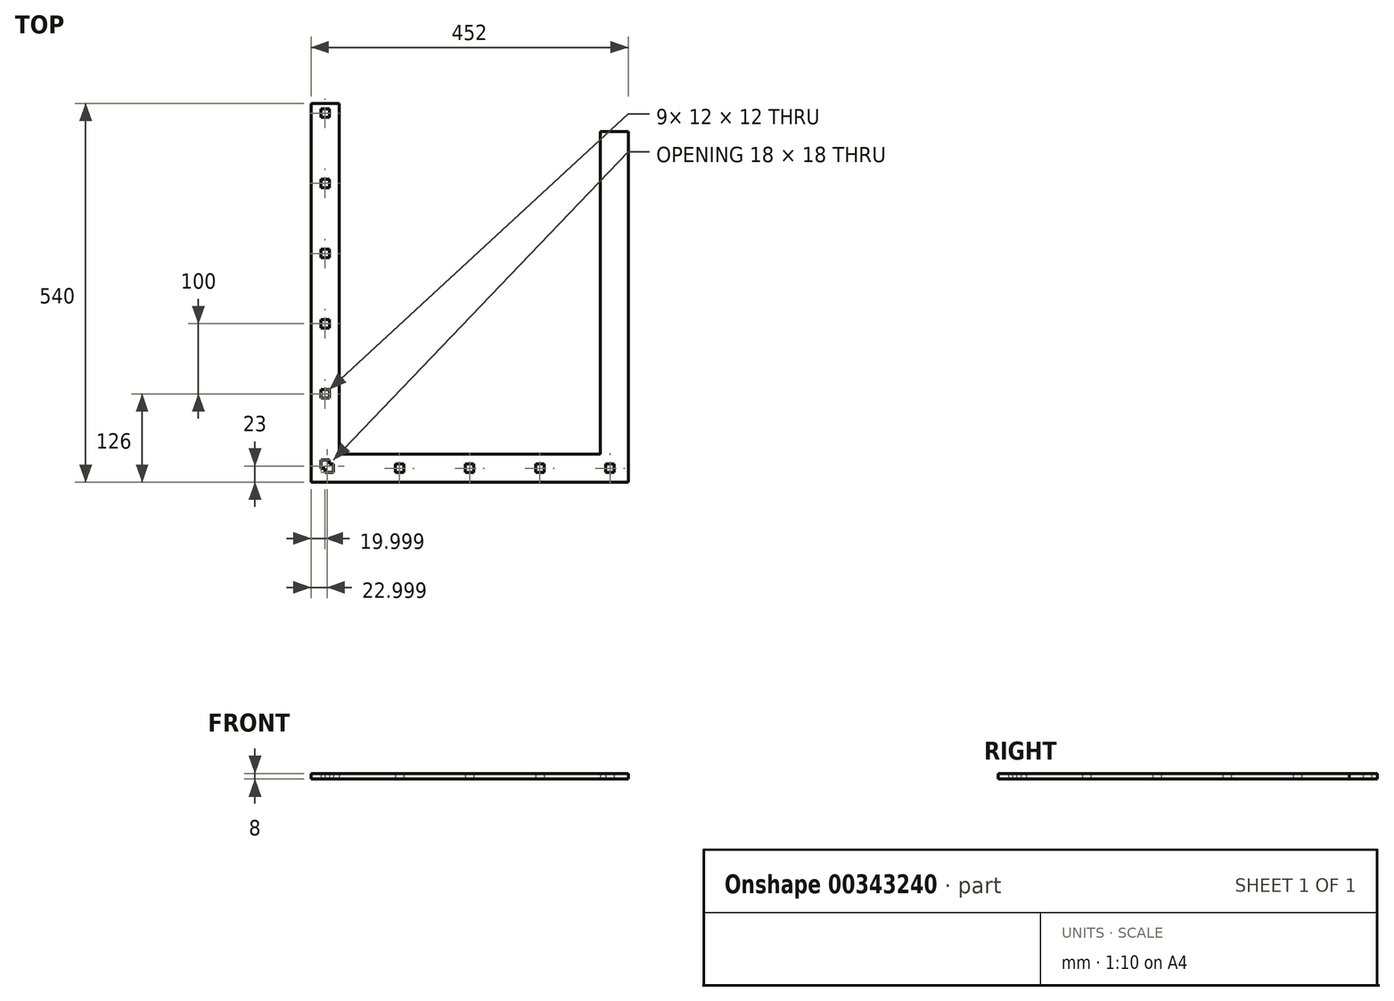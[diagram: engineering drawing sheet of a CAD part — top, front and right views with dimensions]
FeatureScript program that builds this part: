
annotation { "Feature Type Name" : "Feature", "Feature Type Description" : "" }
export const myFeature = defineFeature(function(context is Context, id is Id, definition is map)
    precondition{}
    {
        {
            var Q0;
            Q0=qCreatedBy(makeId("Top.planeOp"),FACE);
            var sketch = newSketch(context, id + "F0", { "sketchPlane" : qUnion([Q0])});
            skLineSegment(sketch, "E0", {"start": v(252.75, -177.36) * mm, "end": v(252.75, 322.64) * mm});
            skLineSegment(sketch, "E1.MirrorCS", {"start": v(252.75, 322.64) * mm, "end": v(212.75, 322.64) * mm});
            skLineSegment(sketch, "E2.MirrorCS", {"start": v(-199.25, -177.36) * mm, "end": v(252.75, -177.36) * mm});
            skLineSegment(sketch, "E3.MirrorCS", {"start": v(232.75, -151.36) * mm, "end": v(232.75, -163.36) * mm});
            skPoint(sketch, "E4.MirrorP", {"position": v(226.75, -157.36) * mm});
            skLineSegment(sketch, "E5.MirrorCS", {"start": v(220.75, -151.36) * mm, "end": v(232.75, -151.36) * mm});
            skLineSegment(sketch, "E6.MirrorCS", {"start": v(220.75, -151.36) * mm, "end": v(220.75, -163.36) * mm});
            skLineSegment(sketch, "E7.MirrorCS", {"start": v(220.75, -163.36) * mm, "end": v(232.75, -163.36) * mm});
            skLineSegment(sketch, "E8.MirrorCS", {"start": v(212.75, -137.36) * mm, "end": v(-159.25, -137.36) * mm});
            skLineSegment(sketch, "E9.MirrorCS", {"start": v(-173.25, -157.36) * mm, "end": v(-185.25, -157.36) * mm});
            skLineSegment(sketch, "E10.MirrorCS", {"start": v(-179.25, -163.36) * mm, "end": v(-167.25, -163.36) * mm});
            skLineSegment(sketch, "E11.MirrorCS", {"start": v(-167.25, -151.36) * mm, "end": v(-167.25, -163.36) * mm});
            skLineSegment(sketch, "E12.MirrorCS", {"start": v(-173.25, -157.36) * mm, "end": v(-173.25, -145.36) * mm});
            skLineSegment(sketch, "E13.MirrorCS", {"start": v(-179.25, -151.36) * mm, "end": v(-179.25, -163.36) * mm});
            skLineSegment(sketch, "E14.MirrorCS", {"start": v(-179.25, -151.36) * mm, "end": v(-167.25, -151.36) * mm});
            skLineSegment(sketch, "E15.MirrorCS", {"start": v(-185.25, -157.36) * mm, "end": v(-185.25, -145.36) * mm});
            skLineSegment(sketch, "E16.MirrorCS", {"start": v(20.75, -151.36) * mm, "end": v(32.75, -151.36) * mm});
            skLineSegment(sketch, "E17.MirrorCS", {"start": v(-173.25, -145.36) * mm, "end": v(-185.25, -145.36) * mm});
            skLineSegment(sketch, "E18.MirrorCS", {"start": v(20.75, -163.36) * mm, "end": v(32.75, -163.36) * mm});
            skLineSegment(sketch, "E19.MirrorCS", {"start": v(20.75, -151.36) * mm, "end": v(20.75, -163.36) * mm});
            skLineSegment(sketch, "E20.MirrorCS", {"start": v(26.75, -177.36) * mm, "end": v(26.75, -137.36) * mm, "construction": true});
            skLineSegment(sketch, "E21.MirrorCS", {"start": v(26.75, -137.36) * mm, "end": v(26.75, -157.36) * mm});
            skLineSegment(sketch, "E22.MirrorCS", {"start": v(-159.25, -137.36) * mm, "end": v(-199.25, -177.36) * mm, "construction": true});
            skLineSegment(sketch, "E23.MirrorCS", {"start": v(-173.25, -157.36) * mm, "end": v(-198.25, -157.36) * mm, "construction": true});
            skLineSegment(sketch, "E24.MirrorCS", {"start": v(32.75, -151.36) * mm, "end": v(32.75, -163.36) * mm});
            skLineSegment(sketch, "E25.MirrorCS", {"start": v(-173.25, -57.36) * mm, "end": v(-173.25, -45.36) * mm});
            skLineSegment(sketch, "E26.MirrorCS", {"start": v(-79.25, -163.36) * mm, "end": v(-67.25, -163.36) * mm});
            skLineSegment(sketch, "E27.MirrorCS", {"start": v(-173.25, -57.36) * mm, "end": v(-185.25, -57.36) * mm});
            skLineSegment(sketch, "E28.MirrorCS", {"start": v(-67.25, -151.36) * mm, "end": v(-67.25, -163.36) * mm});
            skLineSegment(sketch, "E29.MirrorCS", {"start": v(-79.25, -151.36) * mm, "end": v(-67.25, -151.36) * mm});
            skLineSegment(sketch, "E30.MirrorCS", {"start": v(120.75, -151.36) * mm, "end": v(132.75, -151.36) * mm});
            skLineSegment(sketch, "E31.MirrorCS", {"start": v(120.75, -163.36) * mm, "end": v(132.75, -163.36) * mm});
            skLineSegment(sketch, "E32.MirrorCS", {"start": v(120.75, -151.36) * mm, "end": v(120.75, -163.36) * mm});
            skLineSegment(sketch, "E33.MirrorCS", {"start": v(-173.25, -45.36) * mm, "end": v(-185.25, -45.36) * mm});
            skLineSegment(sketch, "E34.MirrorCS", {"start": v(132.75, -151.36) * mm, "end": v(132.75, -163.36) * mm});
            skLineSegment(sketch, "E35.MirrorCS", {"start": v(-185.25, -57.36) * mm, "end": v(-185.25, -45.36) * mm});
            skLineSegment(sketch, "E36.MirrorCS", {"start": v(-79.25, -151.36) * mm, "end": v(-79.25, -163.36) * mm});
            skPoint(sketch, "E37.MirrorP", {"position": v(-173.25, 42.64) * mm});
            skPoint(sketch, "E38.MirrorP", {"position": v(-173.25, -157.36) * mm});
            skPoint(sketch, "E39.MirrorP", {"position": v(-179.25, 48.64) * mm});
            skPoint(sketch, "E40.MirrorP", {"position": v(126.75, -157.36) * mm});
            skLineSegment(sketch, "E41.MirrorCS", {"start": v(26.75, -157.36) * mm, "end": v(-199.25, -157.36) * mm, "construction": true});
            skPoint(sketch, "E42.MirrorP", {"position": v(-179.25, -151.36) * mm});
            skLineSegment(sketch, "E43.MirrorCS", {"start": v(-173.25, -157.36) * mm, "end": v(-173.25, -57.36) * mm, "construction": true});
            skPoint(sketch, "E44.MirrorP", {"position": v(-173.25, -57.36) * mm});
            skPoint(sketch, "E45.MirrorP", {"position": v(26.75, -157.36) * mm});
            skLineSegment(sketch, "E46.MirrorCS", {"start": v(32.75, -163.36) * mm, "end": v(-67.25, -163.36) * mm, "construction": true});
            skLineSegment(sketch, "E47.MirrorCS", {"start": v(32.75, -163.36) * mm, "end": v(132.75, -163.36) * mm, "construction": true});
            skPoint(sketch, "E48.MirrorP", {"position": v(-73.25, -157.36) * mm});
            skPoint(sketch, "E49.MirrorP", {"position": v(-179.25, -51.36) * mm});
            skLineSegment(sketch, "E50.MirrorCS", {"start": v(-185.25, 242.64) * mm, "end": v(-185.25, 254.64) * mm});
            skLineSegment(sketch, "E51.MirrorCS", {"start": v(-173.25, 154.64) * mm, "end": v(-185.25, 154.64) * mm});
            skLineSegment(sketch, "E52.MirrorCS", {"start": v(-185.25, 42.64) * mm, "end": v(-185.25, 54.64) * mm});
            skLineSegment(sketch, "E53.MirrorCS", {"start": v(-173.25, 242.64) * mm, "end": v(-185.25, 242.64) * mm});
            skLineSegment(sketch, "E54.MirrorCS", {"start": v(-173.25, 42.64) * mm, "end": v(-173.25, 54.64) * mm});
            skLineSegment(sketch, "E55.MirrorCS", {"start": v(-185.25, 342.64) * mm, "end": v(-185.25, 354.64) * mm});
            skLineSegment(sketch, "E56.MirrorCS", {"start": v(-173.25, 242.64) * mm, "end": v(-173.25, 254.64) * mm});
            skLineSegment(sketch, "E57.MirrorCS", {"start": v(-173.25, 42.64) * mm, "end": v(-185.25, 42.64) * mm});
            skLineSegment(sketch, "E58.MirrorCS", {"start": v(-173.25, 54.64) * mm, "end": v(-185.25, 54.64) * mm});
            skLineSegment(sketch, "E59.MirrorCS", {"start": v(-173.25, 342.64) * mm, "end": v(-185.25, 342.64) * mm});
            skLineSegment(sketch, "E60.MirrorCS", {"start": v(-173.25, 254.64) * mm, "end": v(-185.25, 254.64) * mm});
            skLineSegment(sketch, "E61.MirrorCS", {"start": v(-173.25, 342.64) * mm, "end": v(-173.25, 354.64) * mm});
            skLineSegment(sketch, "E62.MirrorCS", {"start": v(-185.25, 142.64) * mm, "end": v(-185.25, 154.64) * mm});
            skLineSegment(sketch, "E63.MirrorCS", {"start": v(-173.25, 354.64) * mm, "end": v(-185.25, 354.64) * mm});
            skLineSegment(sketch, "E64.MirrorCS", {"start": v(-173.25, 142.64) * mm, "end": v(-185.25, 142.64) * mm});
            skLineSegment(sketch, "E65.MirrorCS", {"start": v(-173.25, 142.64) * mm, "end": v(-173.25, 154.64) * mm});
            skPoint(sketch, "E66.MirrorP", {"position": v(-179.25, 248.64) * mm});
            skPoint(sketch, "E67.MirrorP", {"position": v(-173.25, 142.64) * mm});
            skPoint(sketch, "E68.MirrorP", {"position": v(-173.25, 242.64) * mm});
            skPoint(sketch, "E69.MirrorP", {"position": v(-179.25, 148.64) * mm});
            skPoint(sketch, "E70.MirrorP", {"position": v(-179.25, 348.64) * mm});
            skPoint(sketch, "E71.MirrorP", {"position": v(-173.25, 342.64) * mm});
            skLineSegment(sketch, "E72", {"start": v(-199.25, 362.64) * mm, "end": v(-159.25, 362.64) * mm});
            skLineSegment(sketch, "E73", {"start": v(-199.25, 362.64) * mm, "end": v(-199.25, -177.36) * mm});
            skLineSegment(sketch, "E74.trimOffspring", {"start": v(-159.25, -137.36) * mm, "end": v(-159.25, 362.64) * mm});
            skLineSegment(sketch, "E75", {"start": v(212.75, 322.64) * mm, "end": v(212.75, -137.36) * mm});
            skSolve(sketch);
        }
        {
            var Q0;
            Q0=makeQuery(id+"F0.imprint","IMPRINT",FACE,{"disambiguationData":[TD([[makeQuery(id+"F0.imprint","IMPRINT",EDGE,{"derivedFrom":sQuery(id+"F0.wireOp",EDGE,"E0")}),1.0]])]});
            extrude(context, id + "F1", {"entities" : qUnion([Q0]), "depth" : 8 * mm});
        }
    });
